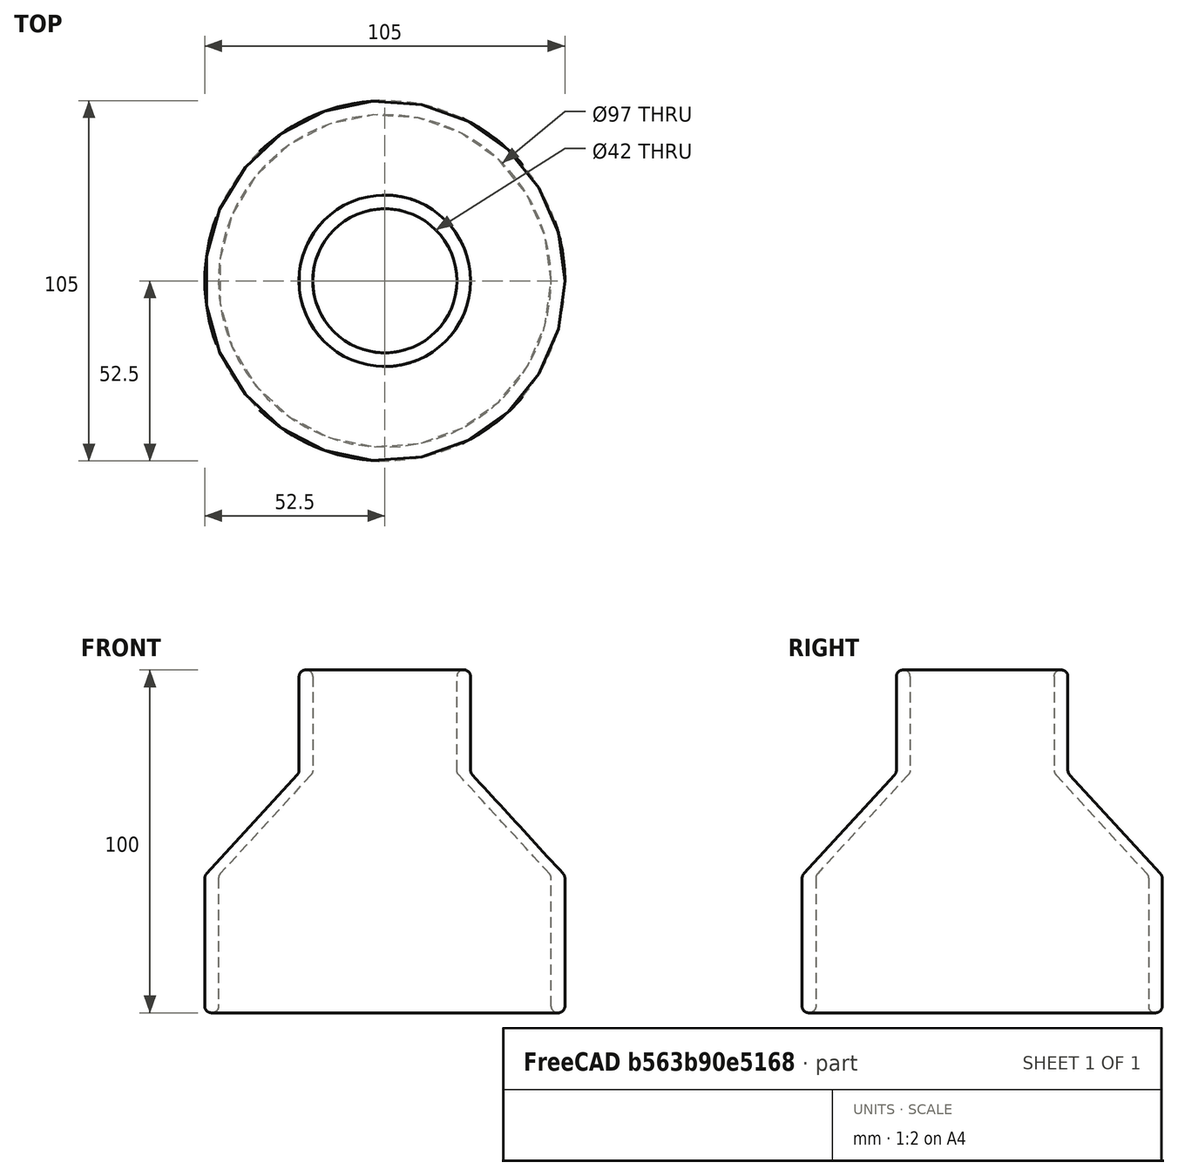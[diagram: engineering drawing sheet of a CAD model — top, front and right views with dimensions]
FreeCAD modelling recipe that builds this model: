
FCSTD DOCUMENT  (FreeCAD 1.0R39109 (Git))
Label: 50to100_single_adapter
License: All rights reserved
LicenseURL: https://en.wikipedia.org/wiki/All_rights_reserved
objects: Sketcher::SketchObject×2, PartDesign::Pad×2, PartDesign::AdditiveLoft×1, PartDesign::Fillet×1, PartDesign::Body×1, Mesh::Feature×1
note: 17 computed .brp shape members not serialized (recipe doc carries the construction recipe); baked Part::Feature solids carry a one-line shape summary decoded from their .brp

FEATURE [Sketcher::SketchObject] Sketch
  ArcFitTolerance = 1e-06
  AttachmentSupport = -> [XY_Plane]
  FullyConstrained = true
  MakeInternals = false
  MapMode = 5
  sketch-geometry (4):
    g0: Circle CenterX=0 CenterY=0 CenterZ=0 NormalX=0 NormalY=0 NormalZ=1 AngleXU=0 Radius=48.5
    g1: Circle CenterX=0 CenterY=0 CenterZ=0 NormalX=0 NormalY=0 NormalZ=1 AngleXU=0 Radius=52.5
    g2: GeomPoint X=48.5 Y=0 Z=0
    g3: GeomPoint X=52.5 Y=0 Z=0
  constraints (8):
    c: Coincident(g0,g-1)
    c: Coincident(g1,g0)
    c: PointOnObject(g2,g0)
    c: PointOnObject(g3,g1)
    c: DistanceX(g2,g3) = 4
    c: Diameter(g1) = 105
    c: Horizontal(g3,g2)
    c: Horizontal(g2,g0)
FEATURE [PartDesign::Pad] Pad
  Direction = (0,0,1)
  Length = 40
  Length2 = 10
  Profile = -> Sketch
  ReferenceAxis = -> Sketch [N_Axis]
  Refine = true
  Suppressed = false
  Type = 0
FEATURE [Sketcher::SketchObject] Sketch001
  ArcFitTolerance = 1e-06
  AttachmentOffset = pos=(0,0,70) rot=(0,0,1;0rad)
  AttachmentSupport = -> [XY_Plane]
  FullyConstrained = true
  MakeInternals = false
  MapMode = 5
  Placement = pos=(0,0,70) rot=(0,0,1;0rad)
  sketch-geometry (4):
    g0: Circle CenterX=0 CenterY=0 CenterZ=0 NormalX=0 NormalY=0 NormalZ=1 AngleXU=0 Radius=25
    g1: Circle CenterX=0 CenterY=0 CenterZ=0 NormalX=0 NormalY=0 NormalZ=1 AngleXU=0 Radius=21
    g2: GeomPoint X=21 Y=0 Z=0
    g3: GeomPoint X=25 Y=0 Z=0
  constraints (8):
    c: Coincident(g1,g0)
    c: Diameter(g0) = 50
    c: PointOnObject(g2,g1)
    c: PointOnObject(g3,g0)
    c: Horizontal(g-1,g3)
    c: Horizontal(g3,g2)
    c: DistanceX(g2,g3) = 4
    c: Coincident(g0,g-1)
FEATURE [PartDesign::AdditiveLoft] AdditiveLoft
  BaseFeature = -> Pad
  Closed = false
  Profile = -> Pad [Face4]
  Refine = true
  Ruled = false
  Sections = -> [Sketch001]
  Suppressed = false
FEATURE [PartDesign::Pad] Pad001
  BaseFeature = -> AdditiveLoft
  Direction = (0,0,1)
  Length = 30
  Length2 = 10
  Profile = -> AdditiveLoft [Face5]
  Refine = true
  Suppressed = false
  Type = 0
FEATURE [PartDesign::Fillet] Fillet
  Base = -> Pad001
  BaseFeature = -> Pad001
  Radius = 1.9
  Refine = true
  SupportTransform = false
  Suppressed = false
  UseAllEdges = true
FEATURE [PartDesign::Body] Body
  AllowCompound = false
  Group = -> [Sketch,Pad,Sketch001,AdditiveLoft,Pad001,Fillet]
  Origin = -> Origin
  Tip = -> Fillet
FEATURE [Mesh::Feature] Mesh  label="Body (Meshed)"
